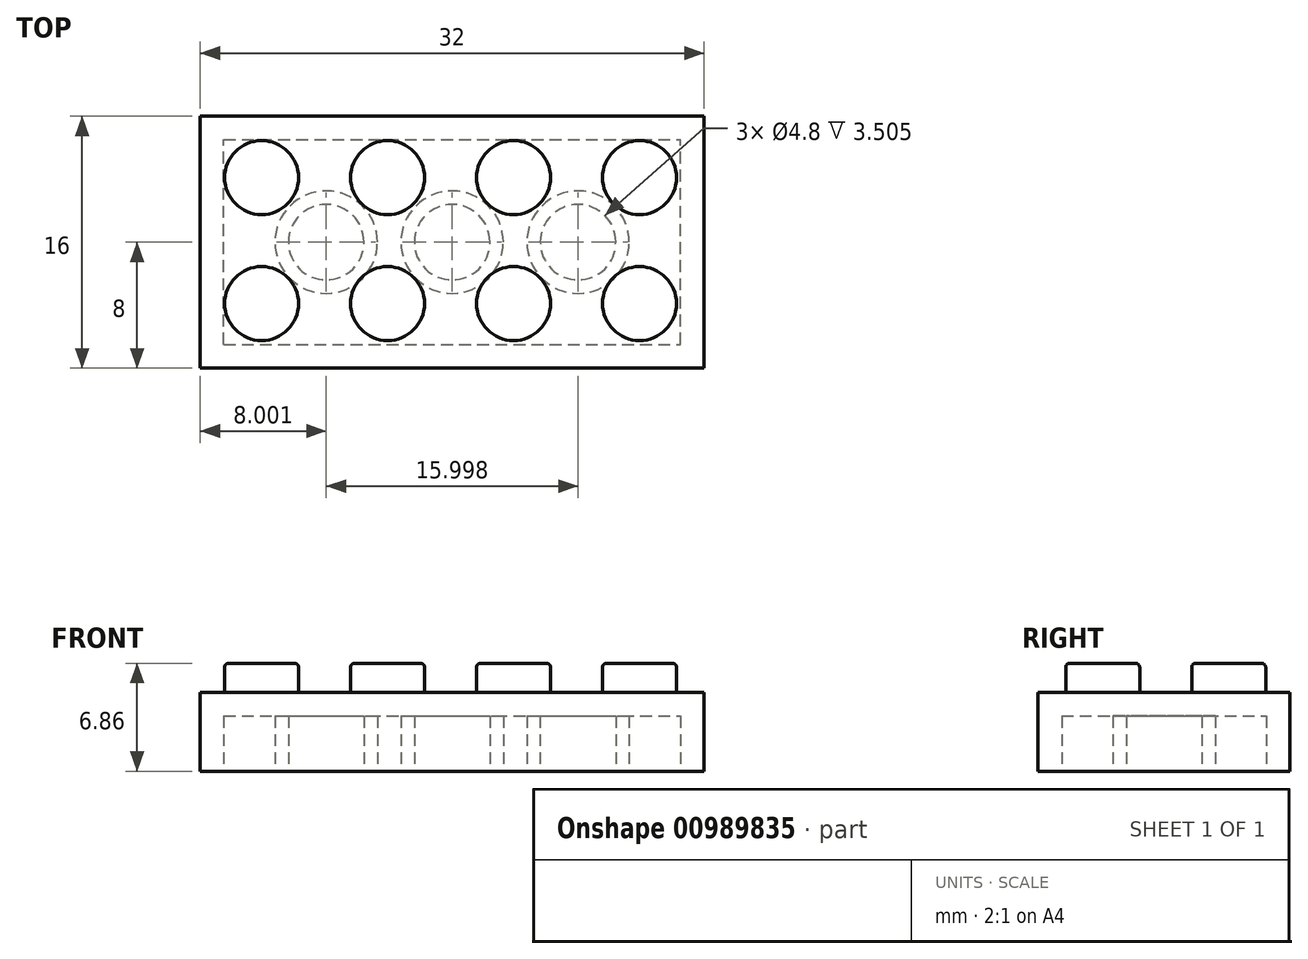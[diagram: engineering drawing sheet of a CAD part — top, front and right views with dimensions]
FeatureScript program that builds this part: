
annotation { "Feature Type Name" : "Feature", "Feature Type Description" : "" }
export const myFeature = defineFeature(function(context is Context, id is Id, definition is map)
    precondition{}
    {
        {
            var Q0;
            Q0=qCreatedBy(makeId("Top.planeOp"),FACE);
            var sketch = newSketch(context, id + "F0", { "sketchPlane" : qUnion([Q0])});
            skLineSegment(sketch, "E0.bottom", {"start": v(0, 0) * mm, "end": v(32, 0) * mm});
            skLineSegment(sketch, "E0.top", {"start": v(0, 16) * mm, "end": v(32, 16) * mm});
            skLineSegment(sketch, "E0.left", {"start": v(0, 0) * mm, "end": v(0, 16) * mm});
            skLineSegment(sketch, "E0.right", {"start": v(32, 0) * mm, "end": v(32, 16) * mm});
            skSolve(sketch);
        }
        {
            var Q0;
            Q0=makeQuery(id+"F0.imprint","IMPRINT",FACE,{"disambiguationData":[TD([[makeQuery(id+"F0.imprint","IMPRINT",EDGE,{"derivedFrom":sQuery(id+"F0.wireOp",EDGE,"E0.bottom")}),1.0]])]});
            extrude(context, id + "F1", {"entities" : qUnion([Q0]), "depth" : 5 * mm, "offsetDistance" : 25.4 * mm});
        }
        {
            var Q0;
            Q0=makeQuery(id+"F1.opExtrude","CAP_FACE",FACE,{"disambiguationData":[OSD([sQuery(id+"F0.wireOp",EDGE,"E0.bottom"),sQuery(id+"F0.wireOp",EDGE,"E0.top"),sQuery(id+"F0.wireOp",EDGE,"E0.left"),sQuery(id+"F0.wireOp",EDGE,"E0.right")])],"isStart":false});
            var sketch = newSketch(context, id + "F2", { "sketchPlane" : qUnion([Q0])});
            skCircle(sketch, "E1", {"center": v(3.9, 12.1) * mm, "radius": 2.35 * mm});
            skCircle(sketch, "E2.0.1.0", {"center": v(3.9, 4.1) * mm, "radius": 2.35 * mm});
            skCircle(sketch, "E2.1.0.0", {"center": v(11.9, 12.1) * mm, "radius": 2.35 * mm});
            skCircle(sketch, "E2.1.1.0", {"center": v(11.9, 4.1) * mm, "radius": 2.35 * mm});
            skCircle(sketch, "E2.2.0.0", {"center": v(19.9, 12.1) * mm, "radius": 2.35 * mm});
            skCircle(sketch, "E2.2.1.0", {"center": v(19.9, 4.1) * mm, "radius": 2.35 * mm});
            skCircle(sketch, "E2.3.0.0", {"center": v(27.9, 12.1) * mm, "radius": 2.35 * mm});
            skCircle(sketch, "E2.3.1.0", {"center": v(27.9, 4.1) * mm, "radius": 2.35 * mm});
            skLineSegment(sketch, "E2.direction1", {"start": v(3.9, 12.1) * mm, "end": v(11.9, 12.1) * mm, "construction": true});
            skLineSegment(sketch, "E2.direction2", {"start": v(3.9, 12.1) * mm, "end": v(3.9, 4.1) * mm, "construction": true});
            skSolve(sketch);
        }
        {
            var Q0;
            Q0=makeQuery(id+"F2.imprint","IMPRINT",FACE,{"disambiguationData":[TD([[makeQuery(id+"F2.imprint","IMPRINT",EDGE,{"derivedFrom":sQuery(id+"F2.wireOp",EDGE,"E2.0.1.0")}),1.0]])]});
            var Q1;
            Q1=makeQuery(id+"F2.imprint","IMPRINT",FACE,{"disambiguationData":[TD([[makeQuery(id+"F2.imprint","IMPRINT",EDGE,{"derivedFrom":sQuery(id+"F2.wireOp",EDGE,"E2.1.1.0")}),1.0]])]});
            var Q2;
            Q2=makeQuery(id+"F2.imprint","IMPRINT",FACE,{"disambiguationData":[TD([[makeQuery(id+"F2.imprint","IMPRINT",EDGE,{"derivedFrom":sQuery(id+"F2.wireOp",EDGE,"E2.2.1.0")}),1.0]])]});
            var Q3;
            Q3=makeQuery(id+"F2.imprint","IMPRINT",FACE,{"disambiguationData":[TD([[makeQuery(id+"F2.imprint","IMPRINT",EDGE,{"derivedFrom":sQuery(id+"F2.wireOp",EDGE,"E1")}),1.0]])]});
            var Q4;
            Q4=makeQuery(id+"F2.imprint","IMPRINT",FACE,{"disambiguationData":[TD([[makeQuery(id+"F2.imprint","IMPRINT",EDGE,{"derivedFrom":sQuery(id+"F2.wireOp",EDGE,"E2.1.0.0")}),1.0]])]});
            var Q5;
            Q5=makeQuery(id+"F2.imprint","IMPRINT",FACE,{"disambiguationData":[TD([[makeQuery(id+"F2.imprint","IMPRINT",EDGE,{"derivedFrom":sQuery(id+"F2.wireOp",EDGE,"E2.2.0.0")}),1.0]])]});
            var Q6;
            Q6=makeQuery(id+"F2.imprint","IMPRINT",FACE,{"disambiguationData":[TD([[makeQuery(id+"F2.imprint","IMPRINT",EDGE,{"derivedFrom":sQuery(id+"F2.wireOp",EDGE,"E2.3.0.0")}),1.0]])]});
            var Q7;
            Q7=makeQuery(id+"F2.imprint","IMPRINT",FACE,{"disambiguationData":[TD([[makeQuery(id+"F2.imprint","IMPRINT",EDGE,{"derivedFrom":sQuery(id+"F2.wireOp",EDGE,"E2.3.1.0")}),1.0]])]});
            extrude(context, id + "F3", {"entities" : qUnion([Q0, Q1, Q2, Q3, Q4, Q5, Q6, Q7]), "operationType" : NewBodyOperationType.ADD, "depth" : 1.85 * mm, "offsetDistance" : 25.4 * mm});
        }
        {
            var Q0;
            Q0=makeQuery(id+"F3.opExtrude","CAP_EDGE",EDGE,{"disambiguationData":[OSD([sQuery(id+"F2.wireOp",EDGE,"E2.0.1.0")])],"isStart":false});
            var Q1;
            Q1=makeQuery(id+"F3.opExtrude","CAP_EDGE",EDGE,{"disambiguationData":[OSD([sQuery(id+"F2.wireOp",EDGE,"E2.1.1.0")])],"isStart":false});
            var Q2;
            Q2=makeQuery(id+"F3.opExtrude","CAP_EDGE",EDGE,{"disambiguationData":[OSD([sQuery(id+"F2.wireOp",EDGE,"E2.2.1.0")])],"isStart":false});
            var Q3;
            Q3=makeQuery(id+"F3.opExtrude","CAP_EDGE",EDGE,{"disambiguationData":[OSD([sQuery(id+"F2.wireOp",EDGE,"E2.3.1.0")])],"isStart":false});
            var Q4;
            Q4=makeQuery(id+"F3.opExtrude","CAP_EDGE",EDGE,{"disambiguationData":[OSD([sQuery(id+"F2.wireOp",EDGE,"E2.3.0.0")])],"isStart":false});
            var Q5;
            Q5=makeQuery(id+"F3.opExtrude","CAP_EDGE",EDGE,{"disambiguationData":[OSD([sQuery(id+"F2.wireOp",EDGE,"E2.2.0.0")])],"isStart":false});
            var Q6;
            Q6=makeQuery(id+"F3.opExtrude","CAP_EDGE",EDGE,{"disambiguationData":[OSD([sQuery(id+"F2.wireOp",EDGE,"E2.1.0.0")])],"isStart":false});
            var Q7;
            Q7=makeQuery(id+"F3.opExtrude","CAP_EDGE",EDGE,{"disambiguationData":[OSD([sQuery(id+"F2.wireOp",EDGE,"E1")])],"isStart":false});
            fillet(context, id + "F4", {"entities" : qUnion([Q0, Q1, Q2, Q3, Q4, Q5, Q6, Q7]), "radius" : .25 * mm, "tangentPropagation" : true, "allowEdgeOverflow" : false});
        }
        {
            var Q0;
            Q0=makeQuery(id+"F1.opExtrude","CAP_FACE",FACE,{"disambiguationData":[OSD([sQuery(id+"F0.wireOp",EDGE,"E0.bottom"),sQuery(id+"F0.wireOp",EDGE,"E0.top"),sQuery(id+"F0.wireOp",EDGE,"E0.left"),sQuery(id+"F0.wireOp",EDGE,"E0.right")])],"isStart":true});
            var sketch = newSketch(context, id + "F5", { "sketchPlane" : qUnion([Q0])});
            skLineSegment(sketch, "E3.0", {"start": v(1.5, -1.5) * mm, "end": v(1.5, -14.5) * mm});
            skLineSegment(sketch, "E3.1", {"start": v(1.5, -1.5) * mm, "end": v(30.5, -1.5) * mm});
            skLineSegment(sketch, "E3.2", {"start": v(30.5, -1.5) * mm, "end": v(30.5, -14.5) * mm});
            skLineSegment(sketch, "E3.3", {"start": v(1.5, -14.5) * mm, "end": v(30.5, -14.5) * mm});
            skLineSegment(sketch, "E4", {"start": v(0, 0) * mm, "end": v(32, -16) * mm, "construction": true});
            skLineSegment(sketch, "E5", {"start": v(32, -16) * mm, "end": v(32, 0) * mm});
            skLineSegment(sketch, "E6", {"start": v(32, 0) * mm, "end": v(0, -16) * mm, "construction": true});
            skCircle(sketch, "E7", {"center": v(16, -8) * mm, "radius": 3.25 * mm});
            skCircle(sketch, "E8", {"center": v(16, -8) * mm, "radius": 2.4 * mm});
            skCircle(sketch, "E9", {"center": v(24, -8) * mm, "radius": 2.4 * mm});
            skCircle(sketch, "E10", {"center": v(24, -8) * mm, "radius": 3.25 * mm});
            skCircle(sketch, "E11", {"center": v(8, -8) * mm, "radius": 2.4 * mm});
            skCircle(sketch, "E12", {"center": v(8, -8) * mm, "radius": 3.25 * mm});
            skSolve(sketch);
        }
        {
            var Q0;
            Q0=makeQuery(id+"F5.imprint","IMPRINT",FACE,{"disambiguationData":[TD([[makeQuery(id+"F5.imprint","IMPRINT",EDGE,{"derivedFrom":sQuery(id+"F5.wireOp",EDGE,"E3.0")}),1.0]])]});
            var Q1;
            Q1=makeQuery(id+"F5.imprint","IMPRINT",FACE,{"disambiguationData":[TD([[makeQuery(id+"F5.imprint","IMPRINT",EDGE,{"derivedFrom":sQuery(id+"F5.wireOp",EDGE,"E9")}),1.0]])]});
            var Q2;
            Q2=makeQuery(id+"F5.imprint","IMPRINT",FACE,{"disambiguationData":[TD([[makeQuery(id+"F5.imprint","IMPRINT",EDGE,{"derivedFrom":sQuery(id+"F5.wireOp",EDGE,"E8")}),1.0]])]});
            var Q3;
            Q3=makeQuery(id+"F5.imprint","IMPRINT",FACE,{"disambiguationData":[TD([[makeQuery(id+"F5.imprint","IMPRINT",EDGE,{"derivedFrom":sQuery(id+"F5.wireOp",EDGE,"E11")}),1.0]])]});
            extrude(context, id + "F6", {"entities" : qUnion([Q0, Q1, Q2, Q3]), "operationType" : NewBodyOperationType.REMOVE, "oppositeDirection" : true, "depth" : 3.5 * mm, "offsetDistance" : 25.4 * mm});
        }
    });
